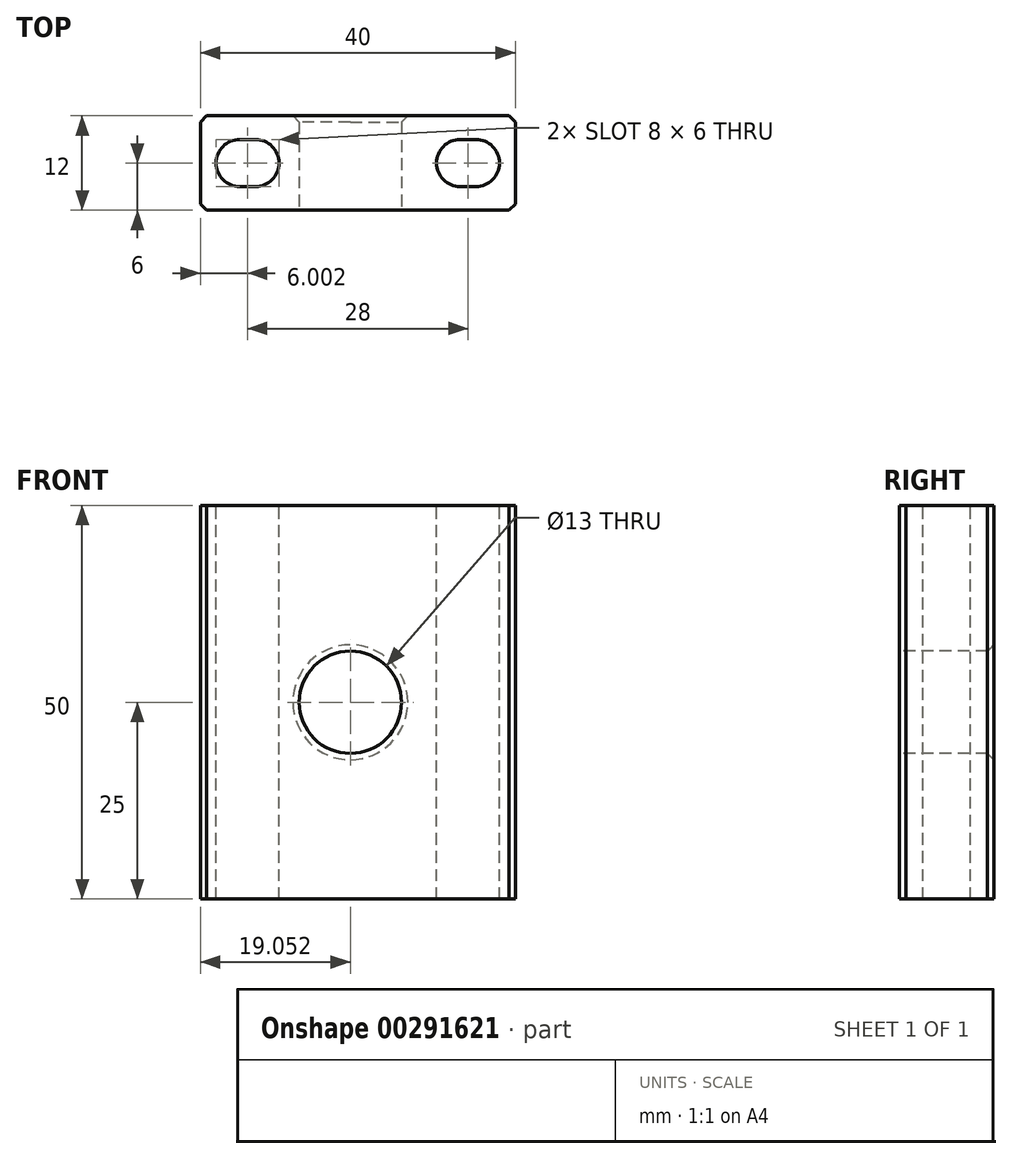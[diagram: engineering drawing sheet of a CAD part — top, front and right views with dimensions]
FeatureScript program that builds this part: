
annotation { "Feature Type Name" : "Feature", "Feature Type Description" : "" }
export const myFeature = defineFeature(function(context is Context, id is Id, definition is map)
    precondition{}
    {
        {
            var Q0;
            Q0=qCreatedBy(makeId("Top.planeOp"),FACE);
            var sketch = newSketch(context, id + "F0", { "sketchPlane" : qUnion([Q0])});
            skLineSegment(sketch, "E0", {"start": v(-32.26, 0) * mm, "end": v(-32.26, 12) * mm});
            skLineSegment(sketch, "E1", {"start": v(7.74, 0) * mm, "end": v(-32.26, 0) * mm});
            skLineSegment(sketch, "E2", {"start": v(-32.26, 12) * mm, "end": v(7.74, 12) * mm});
            skLineSegment(sketch, "E3", {"start": v(7.74, 0) * mm, "end": v(7.74, 12) * mm});
            skSolve(sketch);
        }
        {
            var Q0;
            Q0=makeQuery(id+"F0.imprint","IMPRINT",FACE,{"disambiguationData":[TD([[makeQuery(id+"F0.imprint","IMPRINT",EDGE,{"derivedFrom":sQuery(id+"F0.wireOp",EDGE,"E0")}),-1.0]])]});
            extrude(context, id + "F1", {"entities" : qUnion([Q0]), "depth" : 50 * mm});
        }
        {
            var Q0;
            Q0=makeQuery(id+"F1.opExtrude","CAP_FACE",FACE,{"disambiguationData":[OSD([sQuery(id+"F0.wireOp",EDGE,"E0"),sQuery(id+"F0.wireOp",EDGE,"o2G7Yv12-dZbw-Aksm-vXnR-qdNdU4429cXs"),sQuery(id+"F0.wireOp",EDGE,"KFIwA6Dd-c2ay-AD7S-g6iB-lHe2tFGU7Rjt"),sQuery(id+"F0.wireOp",EDGE,"hYOSYNOn-eQqk-npWH-pDCk-WvwbaqOjX2O7"),sQuery(id+"F0.wireOp",EDGE,"Nx4Z8nex-UuLY-GHDb-3vj8-En5UT6CPUsVi"),sQuery(id+"F0.wireOp",EDGE,"E1")])],"isStart":false});
            var sketch = newSketch(context, id + "F2", { "sketchPlane" : qUnion([Q0])});
            skArc(sketch, "E4", {"start": v(-27.26, 9) * mm, "mid": v(-30.26, 6) * mm, "end": v(-27.26, 3) * mm});
            skArc(sketch, "E5", {"start": v(-25.26, 3) * mm, "mid": v(-22.26, 6) * mm, "end": v(-25.26, 9) * mm});
            skLineSegment(sketch, "E6", {"start": v(-27.26, 9) * mm, "end": v(-25.26, 9) * mm});
            skLineSegment(sketch, "E7", {"start": v(-25.26, 3) * mm, "end": v(-27.26, 3) * mm});
            skArc(sketch, "E8.1.0.0", {"start": v(2.74, 3) * mm, "mid": v(5.74, 6) * mm, "end": v(2.74, 9) * mm});
            skLineSegment(sketch, "E8.1.0.1", {"start": v(0.74, 9) * mm, "end": v(2.74, 9) * mm});
            skArc(sketch, "E8.1.0.3", {"start": v(0.74, 9) * mm, "mid": v(-2.26, 6) * mm, "end": v(0.74, 3) * mm});
            skLineSegment(sketch, "E8.1.0.4", {"start": v(2.74, 3) * mm, "end": v(0.74, 3) * mm});
            skLineSegment(sketch, "E8.direction1", {"start": v(-27.26, 3) * mm, "end": v(0.74, 3) * mm, "construction": true});
            skSolve(sketch);
        }
        {
            var Q0;
            Q0=makeQuery(id+"F2.imprint","IMPRINT",FACE,{"disambiguationData":[TD([[makeQuery(id+"F2.imprint","IMPRINT",EDGE,{"derivedFrom":sQuery(id+"F2.wireOp",EDGE,"E4")}),1.0]])]});
            var Q1;
            Q1=makeQuery(id+"F2.imprint","IMPRINT",FACE,{"disambiguationData":[TD([[makeQuery(id+"F2.imprint","IMPRINT",EDGE,{"derivedFrom":sQuery(id+"F2.wireOp",EDGE,"E8.1.0.0")}),1.0]])]});
            extrude(context, id + "F3", {"entities" : qUnion([Q0, Q1]), "operationType" : NewBodyOperationType.REMOVE, "oppositeDirection" : true, "depth" : 55 * mm});
        }
        {
            var Q0;
            Q0=makeQuery(id+"F1.opExtrude","SWEPT_FACE",FACE,{"disambiguationData":[OSD([sQuery(id+"F0.wireOp",EDGE,"E1")])]});
            var sketch = newSketch(context, id + "F4", { "sketchPlane" : qUnion([Q0])});
            skCircle(sketch, "E9", {"center": v(-13.2, 25) * mm, "radius": 6.5 * mm});
            skSolve(sketch);
        }
        {
            var Q0;
            Q0=makeQuery(id+"F4.imprint","IMPRINT",FACE,{"disambiguationData":[TD([[makeQuery(id+"F4.imprint","IMPRINT",EDGE,{"derivedFrom":sQuery(id+"F4.wireOp",EDGE,"E9")}),1.0]])]});
            extrude(context, id + "F5", {"entities" : qUnion([Q0]), "operationType" : NewBodyOperationType.REMOVE, "oppositeDirection" : true, "depth" : 13 * mm});
        }
        {
            var Q0;
            Q0=makeQuery(id+"F1.opExtrude","SWEPT_EDGE",EDGE,{"disambiguationData":[OSD([sQuery(id+"F0.wireOp",EDGE,"E1"),sQuery(id+"F0.wireOp",EDGE,"E3")])]});
            var Q1;
            Q1=makeQuery(id+"F1.opExtrude","SWEPT_EDGE",EDGE,{"disambiguationData":[OSD([sQuery(id+"F0.wireOp",EDGE,"E3"),sQuery(id+"F0.wireOp",EDGE,"v4A9VM9Y-L8iL-7CuQ-0jf7-fQpHDtcfk9JR")])]});
            var Q2;
            Q2=makeQuery(id+"F1.opExtrude","SWEPT_EDGE",EDGE,{"disambiguationData":[OSD([sQuery(id+"F0.wireOp",EDGE,"v4A9VM9Y-L8iL-7CuQ-0jf7-fQpHDtcfk9JR"),sQuery(id+"F0.wireOp",EDGE,"G6UKNEKG-hcxT-9y6d-61yz-wjkH6LF0nyjn")])]});
            var Q3;
            Q3=makeQuery(id+"F1.opExtrude","SWEPT_EDGE",EDGE,{"disambiguationData":[OSD([sQuery(id+"F0.wireOp",EDGE,"k8x1jUSQ-Bb0A-k1Qb-C6Zh-FND75i37FcIW"),sQuery(id+"F0.wireOp",EDGE,"G6UKNEKG-hcxT-9y6d-61yz-wjkH6LF0nyjn")])]});
            var Q4;
            Q4=makeQuery(id+"F1.opExtrude","SWEPT_EDGE",EDGE,{"disambiguationData":[OSD([sQuery(id+"F0.wireOp",EDGE,"E0"),sQuery(id+"F0.wireOp",EDGE,"E2")])]});
            var Q5;
            Q5=makeQuery(id+"F1.opExtrude","SWEPT_EDGE",EDGE,{"disambiguationData":[OSD([sQuery(id+"F0.wireOp",EDGE,"E0"),sQuery(id+"F0.wireOp",EDGE,"E1")])]});
            var Q6;
            {var subQ0=sQuery(id+"F0.wireOp",EDGE,"Iti7kjTL-CILF-zkgD-OpJd-5bMqSwruP2lm");var subQ1=sQuery(id+"F0.wireOp",EDGE,"E2");Q6=makeQuery(id+"F5.boolean.opBoolean","SPLIT",EDGE,{"disambiguationData":[TD([makeQuery(id+"F1.opExtrude","CAP_FACE",FACE,{"disambiguationData":[OSD([sQuery(id+"F0.wireOp",EDGE,"E0"),sQuery(id+"F0.wireOp",EDGE,"E1"),subQ1,sQuery(id+"F0.wireOp",EDGE,"k8x1jUSQ-Bb0A-k1Qb-C6Zh-FND75i37FcIW"),subQ0,sQuery(id+"F0.wireOp",EDGE,"E3"),sQuery(id+"F0.wireOp",EDGE,"v4A9VM9Y-L8iL-7CuQ-0jf7-fQpHDtcfk9JR"),sQuery(id+"F0.wireOp",EDGE,"G6UKNEKG-hcxT-9y6d-61yz-wjkH6LF0nyjn")])],"isStart":false})])],"derivedFrom":makeQuery(id+"F1.opExtrude","SWEPT_EDGE",EDGE,{"disambiguationData":[OSD([subQ1,subQ0])]})});}
            var Q7;
            {var subQ0=sQuery(id+"F0.wireOp",EDGE,"Iti7kjTL-CILF-zkgD-OpJd-5bMqSwruP2lm");var subQ1=sQuery(id+"F0.wireOp",EDGE,"E2");Q7=makeQuery(id+"F5.boolean.opBoolean","SPLIT",EDGE,{"disambiguationData":[TD([makeQuery(id+"F1.opExtrude","CAP_FACE",FACE,{"disambiguationData":[OSD([sQuery(id+"F0.wireOp",EDGE,"E0"),sQuery(id+"F0.wireOp",EDGE,"E1"),subQ1,sQuery(id+"F0.wireOp",EDGE,"k8x1jUSQ-Bb0A-k1Qb-C6Zh-FND75i37FcIW"),subQ0,sQuery(id+"F0.wireOp",EDGE,"E3"),sQuery(id+"F0.wireOp",EDGE,"v4A9VM9Y-L8iL-7CuQ-0jf7-fQpHDtcfk9JR"),sQuery(id+"F0.wireOp",EDGE,"G6UKNEKG-hcxT-9y6d-61yz-wjkH6LF0nyjn")])],"isStart":true})])],"derivedFrom":makeQuery(id+"F1.opExtrude","SWEPT_EDGE",EDGE,{"disambiguationData":[OSD([subQ1,subQ0])]})});}
            var Q8;
            Q8=makeQuery(id+"F1.opExtrude","SWEPT_EDGE",EDGE,{"disambiguationData":[OSD([sQuery(id+"F0.wireOp",EDGE,"k8x1jUSQ-Bb0A-k1Qb-C6Zh-FND75i37FcIW"),sQuery(id+"F0.wireOp",EDGE,"Iti7kjTL-CILF-zkgD-OpJd-5bMqSwruP2lm")])]});
            var Q9;
            Q9=makeQuery(id+"F5.boolean.opBoolean","INTERSECT",EDGE,{"derivedFrom":[makeQuery(id+"F1.opExtrude","SWEPT_FACE",FACE,{"disambiguationData":[OSD([sQuery(id+"F0.wireOp",EDGE,"E2")])]}),makeQuery(id+"F5.opExtrude","SWEPT_FACE",FACE,{"disambiguationData":[OSD([sQuery(id+"F4.wireOp",EDGE,"E9")])]})]});
            var Q10;
            Q10=makeQuery(id+"F5.boolean.opBoolean","COPY",EDGE,{"derivedFrom":makeQuery(id+"F5.opExtrude","CAP_EDGE",EDGE,{"disambiguationData":[OSD([sQuery(id+"F4.wireOp",EDGE,"E9")])],"isStart":true})});
            chamfer(context, id + "F6", {"entities" : qUnion([Q0, Q1, Q2, Q3, Q4, Q5, Q6, Q7, Q8, Q9, Q10]), "width" : 0.8 * mm, "tangentPropagation" : true});
        }
    });
